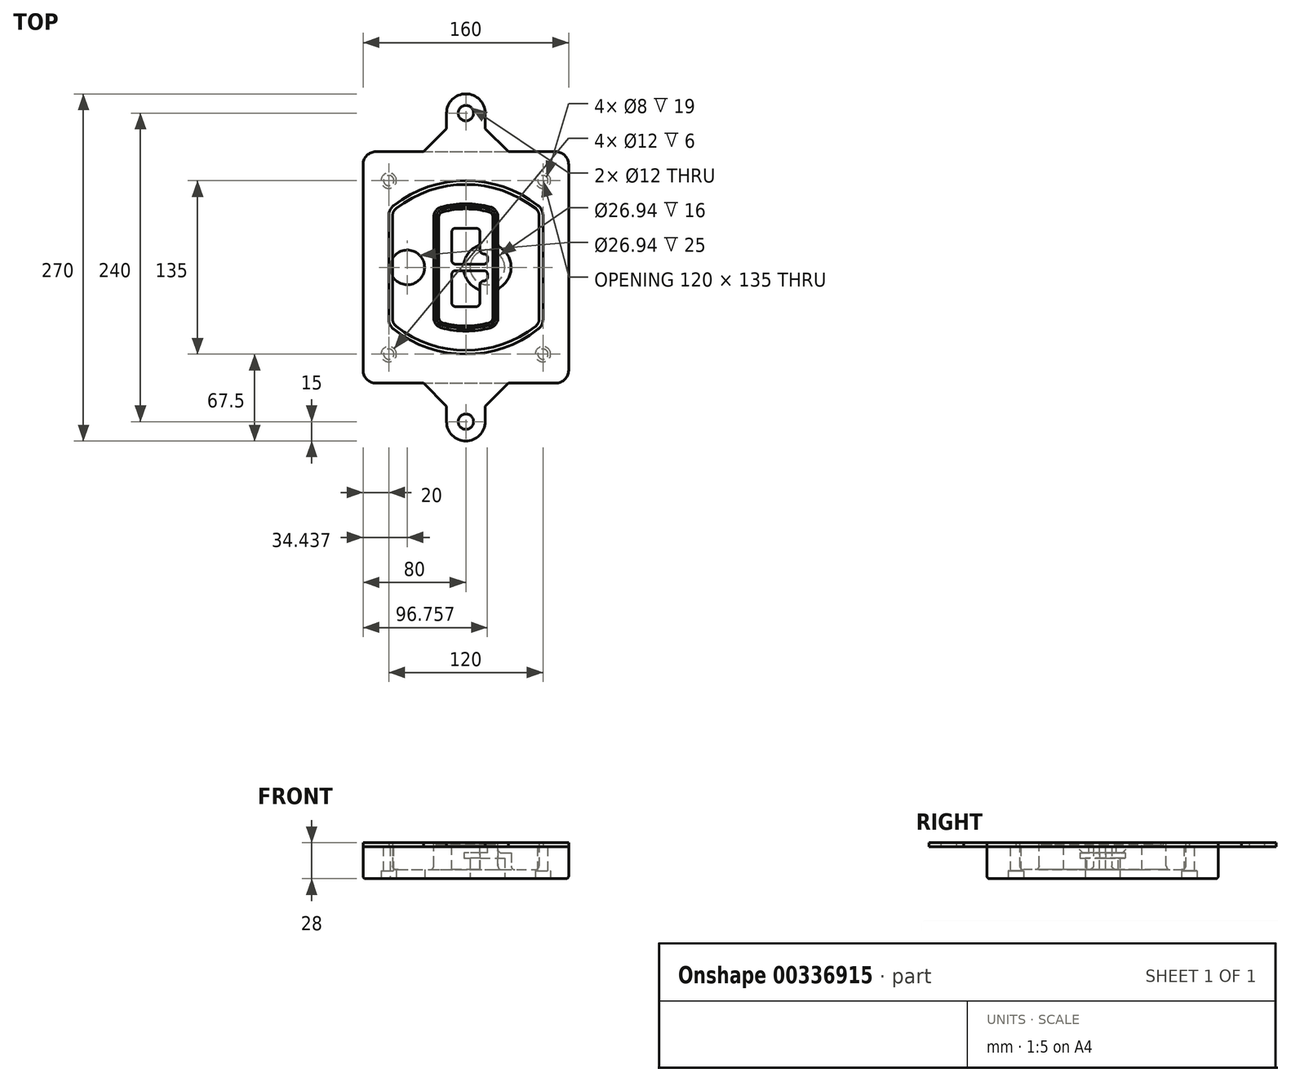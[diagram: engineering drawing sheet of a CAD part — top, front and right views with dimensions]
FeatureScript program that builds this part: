
annotation { "Feature Type Name" : "Feature", "Feature Type Description" : "" }
export const myFeature = defineFeature(function(context is Context, id is Id, definition is map)
    precondition{}
    {
        {
            var Q0;
            Q0=qCreatedBy(makeId("Top.planeOp"),FACE);
            var sketch = newSketch(context, id + "F0", { "sketchPlane" : qUnion([Q0])});
            skPoint(sketch, "E0.rect.middle", {"position": v(0, 0) * mm});
            skLineSegment(sketch, "E1.bottom", {"start": v(-70, -90) * mm, "end": v(70, -90) * mm});
            skLineSegment(sketch, "E1.top", {"start": v(-70, 90) * mm, "end": v(70, 90) * mm});
            skLineSegment(sketch, "E1.left", {"start": v(-80, -80) * mm, "end": v(-80, 80) * mm});
            skLineSegment(sketch, "E1.right", {"start": v(80, -80) * mm, "end": v(80, 80) * mm});
            skLineSegment(sketch, "E2", {"start": v(-80, 90) * mm, "end": v(80, -90) * mm, "construction": true});
            skLineSegment(sketch, "E3", {"start": v(80, 90) * mm, "end": v(-80, -90) * mm, "construction": true});
            skCircle(sketch, "E4", {"center": v(-60, 67.5) * mm, "radius": 4 * mm});
            skCircle(sketch, "E5", {"center": v(60, 67.5) * mm, "radius": 4 * mm});
            skCircle(sketch, "E6", {"center": v(60, -67.5) * mm, "radius": 4 * mm});
            skCircle(sketch, "E7", {"center": v(-60, -67.5) * mm, "radius": 4 * mm});
            skLineSegment(sketch, "E8", {"start": v(-60, 67.5) * mm, "end": v(60, 67.5) * mm, "construction": true});
            skLineSegment(sketch, "E9", {"start": v(60, 67.5) * mm, "end": v(60, -67.5) * mm, "construction": true});
            skLineSegment(sketch, "E10", {"start": v(60, -67.5) * mm, "end": v(-60, -67.5) * mm, "construction": true});
            skLineSegment(sketch, "E11", {"start": v(-60, -67.5) * mm, "end": v(-60, 67.5) * mm, "construction": true});
            skLineSegment(sketch, "E12", {"start": v(-60, 40.3) * mm, "end": v(-60, -40.3) * mm});
            skLineSegment(sketch, "E13", {"start": v(60, 40.3) * mm, "end": v(60, -40.3) * mm});
            skArc(sketch, "E14", {"start": v(56.15, 48.18) * mm, "mid": v(0, 67.5) * mm, "end": v(-56.15, 48.18) * mm});
            skArc(sketch, "E15", {"start": v(-56.15, -48.18) * mm, "mid": v(0, -67.5) * mm, "end": v(56.15, -48.18) * mm});
            skLineSegment(sketch, "E16", {"start": v(-60, 0) * mm, "end": v(60, 0) * mm, "construction": true});
            skPoint(sketch, "E17.visualSharp", {"position": v(-60, -45) * mm});
            skArc(sketch, "E17.filletArc", {"start": v(-60, -40.3) * mm, "mid": v(-58.99, -44.68) * mm, "end": v(-56.15, -48.18) * mm});
            skPoint(sketch, "E18.visualSharp", {"position": v(-60, 45) * mm});
            skArc(sketch, "E18.filletArc", {"start": v(-56.15, 48.18) * mm, "mid": v(-58.99, 44.68) * mm, "end": v(-60, 40.3) * mm});
            skPoint(sketch, "E19.visualSharp", {"position": v(60, 45) * mm});
            skArc(sketch, "E19.filletArc", {"start": v(60, 40.3) * mm, "mid": v(58.99, 44.68) * mm, "end": v(56.15, 48.18) * mm});
            skPoint(sketch, "E20.visualSharp", {"position": v(60, -45) * mm});
            skArc(sketch, "E20.filletArc", {"start": v(56.15, -48.18) * mm, "mid": v(58.99, -44.68) * mm, "end": v(60, -40.3) * mm});
            skPoint(sketch, "E21.visualSharp", {"position": v(-80, 90) * mm});
            skArc(sketch, "E21.filletArc", {"start": v(-70, 90) * mm, "mid": v(-77.07, 87.07) * mm, "end": v(-80, 80) * mm});
            skPoint(sketch, "E22.visualSharp", {"position": v(80, 90) * mm});
            skArc(sketch, "E22.filletArc", {"start": v(80, 80) * mm, "mid": v(77.07, 87.07) * mm, "end": v(70, 90) * mm});
            skPoint(sketch, "E23.visualSharp", {"position": v(80, -90) * mm});
            skArc(sketch, "E23.filletArc", {"start": v(70, -90) * mm, "mid": v(77.07, -87.07) * mm, "end": v(80, -80) * mm});
            skPoint(sketch, "E24.visualSharp", {"position": v(-80, -90) * mm});
            skArc(sketch, "E24.filletArc", {"start": v(-80, -80) * mm, "mid": v(-77.07, -87.07) * mm, "end": v(-70, -90) * mm});
            skArc(sketch, "E25.0", {"start": v(57, 40.3) * mm, "mid": v(56.3, 43.36) * mm, "end": v(54.3, 45.81) * mm});
            skLineSegment(sketch, "E25.1", {"start": v(57, 40.3) * mm, "end": v(57, -40.3) * mm});
            skArc(sketch, "E25.2", {"start": v(54.3, -45.81) * mm, "mid": v(56.3, -43.36) * mm, "end": v(57, -40.3) * mm});
            skArc(sketch, "E25.3", {"start": v(-54.3, -45.81) * mm, "mid": v(0, -64.5) * mm, "end": v(54.3, -45.81) * mm});
            skArc(sketch, "E25.4", {"start": v(-57, -40.3) * mm, "mid": v(-56.3, -43.36) * mm, "end": v(-54.3, -45.81) * mm});
            skArc(sketch, "E25.5", {"start": v(54.3, 45.81) * mm, "mid": v(0, 64.5) * mm, "end": v(-54.3, 45.81) * mm});
            skLineSegment(sketch, "E25.6", {"start": v(-57, 40.3) * mm, "end": v(-57, -40.3) * mm});
            skArc(sketch, "E25.7", {"start": v(-54.3, 45.81) * mm, "mid": v(-56.3, 43.36) * mm, "end": v(-57, 40.3) * mm});
            skArc(sketch, "E26.0", {"start": v(-58.62, 51.33) * mm, "mid": v(-62.58, 46.43) * mm, "end": v(-64, 40.3) * mm});
            skArc(sketch, "E26.1", {"start": v(58.62, 51.33) * mm, "mid": v(0, 71.5) * mm, "end": v(-58.62, 51.33) * mm});
            skArc(sketch, "E26.2", {"start": v(64, 40.3) * mm, "mid": v(62.58, 46.43) * mm, "end": v(58.62, 51.33) * mm});
            skLineSegment(sketch, "E26.3", {"start": v(64, 40.3) * mm, "end": v(64, -40.3) * mm});
            skArc(sketch, "E26.4", {"start": v(58.62, -51.33) * mm, "mid": v(62.58, -46.43) * mm, "end": v(64, -40.3) * mm});
            skLineSegment(sketch, "E26.5", {"start": v(-64, 40.3) * mm, "end": v(-64, -40.3) * mm});
            skArc(sketch, "E26.6", {"start": v(-58.62, -51.33) * mm, "mid": v(0, -71.5) * mm, "end": v(58.62, -51.33) * mm});
            skArc(sketch, "E26.7", {"start": v(-64, -40.3) * mm, "mid": v(-62.58, -46.43) * mm, "end": v(-58.62, -51.33) * mm});
            skSolve(sketch);
        }
        {
            var Q0;
            Q0=makeQuery(id+"F0.imprint","IMPRINT",FACE,{"disambiguationData":[TD([[makeQuery(id+"F0.imprint","IMPRINT",EDGE,{"derivedFrom":sQuery(id+"F0.wireOp",EDGE,"E1.bottom")}),1.0]])]});
            var Q1;
            Q1=makeQuery(id+"F0.imprint","IMPRINT",FACE,{"disambiguationData":[TD([[makeQuery(id+"F0.imprint","IMPRINT",EDGE,{"derivedFrom":sQuery(id+"F0.wireOp",EDGE,"E12")}),1.0]])]});
            var Q2;
            Q2=makeQuery(id+"F0.imprint","IMPRINT",FACE,{"disambiguationData":[TD([[makeQuery(id+"F0.imprint","IMPRINT",EDGE,{"derivedFrom":sQuery(id+"F0.wireOp",EDGE,"E25.0")}),1.0]])]});
            var Q3;
            Q3=makeQuery(id+"F0.imprint","IMPRINT",FACE,{"disambiguationData":[TD([[makeQuery(id+"F0.imprint","IMPRINT",EDGE,{"derivedFrom":sQuery(id+"F0.wireOp",EDGE,"E12")}),-1.0]])]});
            extrude(context, id + "F1", {"entities" : qUnion([Q0, Q1, Q2, Q3]), "oppositeDirection" : true, "depth" : 25 * mm});
        }
        {
            var Q0;
            Q0=makeQuery(id+"F0.imprint","IMPRINT",FACE,{"disambiguationData":[TD([[makeQuery(id+"F0.imprint","IMPRINT",EDGE,{"derivedFrom":sQuery(id+"F0.wireOp",EDGE,"E12")}),1.0]])]});
            extrude(context, id + "F2", {"entities" : qUnion([Q0]), "operationType" : NewBodyOperationType.ADD, "depth" : 3 * mm});
        }
        {
            var Q0;
            Q0=makeQuery(id+"F0.imprint","IMPRINT",FACE,{"disambiguationData":[TD([[makeQuery(id+"F0.imprint","IMPRINT",EDGE,{"derivedFrom":sQuery(id+"F0.wireOp",EDGE,"E25.0")}),1.0]])]});
            extrude(context, id + "F3", {"entities" : qUnion([Q0]), "operationType" : NewBodyOperationType.REMOVE, "oppositeDirection" : true, "depth" : 18 * mm});
        }
        {
            var Q0;
            Q0=makeQuery(id+"F2.opExtrude","CAP_FACE",FACE,{"disambiguationData":[OSD([sQuery(id+"F0.wireOp",EDGE,"E12"),sQuery(id+"F0.wireOp",EDGE,"E13"),sQuery(id+"F0.wireOp",EDGE,"E14"),sQuery(id+"F0.wireOp",EDGE,"E15"),sQuery(id+"F0.wireOp",EDGE,"E17.filletArc"),sQuery(id+"F0.wireOp",EDGE,"E18.filletArc"),sQuery(id+"F0.wireOp",EDGE,"E19.filletArc"),sQuery(id+"F0.wireOp",EDGE,"E20.filletArc"),sQuery(id+"F0.wireOp",EDGE,"E25.0"),sQuery(id+"F0.wireOp",EDGE,"E25.1"),sQuery(id+"F0.wireOp",EDGE,"E25.2"),sQuery(id+"F0.wireOp",EDGE,"E25.3"),sQuery(id+"F0.wireOp",EDGE,"E25.4"),sQuery(id+"F0.wireOp",EDGE,"E25.5"),sQuery(id+"F0.wireOp",EDGE,"E25.6"),sQuery(id+"F0.wireOp",EDGE,"E25.7")])],"isStart":false});
            var sketch = newSketch(context, id + "F4", { "sketchPlane" : qUnion([Q0])});
            skArc(sketch, "E27.0", {"start": v(-19.08, -46.97) * mm, "mid": v(0, -49.5) * mm, "end": v(19.08, -46.97) * mm});
            skArc(sketch, "E28.0", {"start": v(19.08, 46.97) * mm, "mid": v(0, 49.5) * mm, "end": v(-19.08, 46.97) * mm});
            skLineSegment(sketch, "E29", {"start": v(-25, 39.25) * mm, "end": v(-25, -39.25) * mm});
            skLineSegment(sketch, "E30", {"start": v(25, 39.25) * mm, "end": v(25, -39.25) * mm});
            skLineSegment(sketch, "E31", {"start": v(-25, 45.1) * mm, "end": v(25, 45.1) * mm, "construction": true});
            skLineSegment(sketch, "E32", {"start": v(-25, -45.1) * mm, "end": v(25, -45.1) * mm, "construction": true});
            skPoint(sketch, "E33.visualSharp", {"position": v(-25, 45.1) * mm});
            skArc(sketch, "E33.filletArc", {"start": v(-19.08, 46.97) * mm, "mid": v(-23.35, 44.11) * mm, "end": v(-25, 39.25) * mm});
            skPoint(sketch, "E34.visualSharp", {"position": v(25, 45.1) * mm});
            skArc(sketch, "E34.filletArc", {"start": v(25, 39.25) * mm, "mid": v(23.35, 44.11) * mm, "end": v(19.08, 46.97) * mm});
            skPoint(sketch, "E35.visualSharp", {"position": v(25, -45.1) * mm});
            skArc(sketch, "E35.filletArc", {"start": v(19.08, -46.97) * mm, "mid": v(23.35, -44.11) * mm, "end": v(25, -39.25) * mm});
            skPoint(sketch, "E36.visualSharp", {"position": v(-25, -45.1) * mm});
            skArc(sketch, "E36.filletArc", {"start": v(-25, -39.25) * mm, "mid": v(-23.35, -44.11) * mm, "end": v(-19.08, -46.97) * mm});
            skArc(sketch, "E37.0", {"start": v(54.3, 45.81) * mm, "mid": v(0, 64.5) * mm, "end": v(-54.3, 45.81) * mm});
            skArc(sketch, "E37.1", {"start": v(-54.3, 45.81) * mm, "mid": v(-56.3, 43.36) * mm, "end": v(-57, 40.3) * mm});
            skLineSegment(sketch, "E37.2", {"start": v(-57, 40.3) * mm, "end": v(-57, -40.3) * mm});
            skArc(sketch, "E37.3", {"start": v(-57, -40.3) * mm, "mid": v(-56.3, -43.36) * mm, "end": v(-54.3, -45.81) * mm});
            skArc(sketch, "E37.4", {"start": v(-54.3, -45.81) * mm, "mid": v(0, -64.5) * mm, "end": v(54.3, -45.81) * mm});
            skArc(sketch, "E37.5", {"start": v(54.3, -45.81) * mm, "mid": v(56.3, -43.36) * mm, "end": v(57, -40.3) * mm});
            skLineSegment(sketch, "E37.6", {"start": v(57, 40.3) * mm, "end": v(57, -40.3) * mm});
            skArc(sketch, "E37.7", {"start": v(57, 40.3) * mm, "mid": v(56.3, 43.36) * mm, "end": v(54.3, 45.81) * mm});
            skLineSegment(sketch, "E38.0", {"start": v(23, 39.25) * mm, "end": v(23, -39.25) * mm});
            skArc(sketch, "E38.1", {"start": v(18.56, -45.04) * mm, "mid": v(21.76, -42.9) * mm, "end": v(23, -39.25) * mm});
            skArc(sketch, "E38.2", {"start": v(-18.56, -45.04) * mm, "mid": v(0, -47.5) * mm, "end": v(18.56, -45.04) * mm});
            skArc(sketch, "E38.3", {"start": v(-23, -39.25) * mm, "mid": v(-21.76, -42.9) * mm, "end": v(-18.56, -45.04) * mm});
            skLineSegment(sketch, "E38.4", {"start": v(-23, 39.25) * mm, "end": v(-23, -39.25) * mm});
            skArc(sketch, "E38.5", {"start": v(23, 39.25) * mm, "mid": v(21.76, 42.9) * mm, "end": v(18.56, 45.04) * mm});
            skArc(sketch, "E38.6", {"start": v(-18.56, 45.04) * mm, "mid": v(-21.76, 42.9) * mm, "end": v(-23, 39.25) * mm});
            skArc(sketch, "E38.7", {"start": v(18.56, 45.04) * mm, "mid": v(0, 47.5) * mm, "end": v(-18.56, 45.04) * mm});
            skArc(sketch, "E39.0", {"start": v(21, 39.25) * mm, "mid": v(20.18, 41.68) * mm, "end": v(18.04, 43.1) * mm});
            skLineSegment(sketch, "E39.1", {"start": v(21, 39.25) * mm, "end": v(21, -39.25) * mm});
            skArc(sketch, "E39.2", {"start": v(18.04, -43.1) * mm, "mid": v(20.18, -41.68) * mm, "end": v(21, -39.25) * mm});
            skArc(sketch, "E39.3", {"start": v(-18.04, -43.1) * mm, "mid": v(0, -45.5) * mm, "end": v(18.04, -43.1) * mm});
            skArc(sketch, "E39.4", {"start": v(-21, -39.25) * mm, "mid": v(-20.18, -41.68) * mm, "end": v(-18.04, -43.1) * mm});
            skArc(sketch, "E39.5", {"start": v(18.04, 43.1) * mm, "mid": v(0, 45.5) * mm, "end": v(-18.04, 43.1) * mm});
            skLineSegment(sketch, "E39.6", {"start": v(-21, 39.25) * mm, "end": v(-21, -39.25) * mm});
            skArc(sketch, "E39.7", {"start": v(-18.04, 43.1) * mm, "mid": v(-20.18, 41.68) * mm, "end": v(-21, 39.25) * mm});
            skLineSegment(sketch, "E40", {"start": v(-25, 0) * mm, "end": v(25, 0) * mm, "construction": true});
            skLineSegment(sketch, "E41", {"start": v(-11, 5.5) * mm, "end": v(-11, 27.5) * mm});
            skLineSegment(sketch, "E42", {"start": v(-8, 30.5) * mm, "end": v(8, 30.5) * mm});
            skLineSegment(sketch, "E43", {"start": v(11, 27.5) * mm, "end": v(11, 13.5) * mm});
            skLineSegment(sketch, "E44", {"start": v(14, 10.5) * mm, "end": v(14, 10.5) * mm});
            skLineSegment(sketch, "E45", {"start": v(17, 7.5) * mm, "end": v(17, 5.5) * mm});
            skLineSegment(sketch, "E46", {"start": v(14, 2.5) * mm, "end": v(-8, 2.5) * mm});
            skPoint(sketch, "E47.visualSharp", {"position": v(-11, 30.5) * mm});
            skArc(sketch, "E47.filletArc", {"start": v(-8, 30.5) * mm, "mid": v(-10.12, 29.62) * mm, "end": v(-11, 27.5) * mm});
            skPoint(sketch, "E48.visualSharp", {"position": v(11, 30.5) * mm});
            skArc(sketch, "E48.filletArc", {"start": v(11, 27.5) * mm, "mid": v(10.12, 29.62) * mm, "end": v(8, 30.5) * mm});
            skPoint(sketch, "E49.visualSharp", {"position": v(11, 10.5) * mm});
            skArc(sketch, "E49.filletArc", {"start": v(11, 13.5) * mm, "mid": v(11.88, 11.38) * mm, "end": v(14, 10.5) * mm});
            skPoint(sketch, "E50.visualSharp", {"position": v(17, 10.5) * mm});
            skArc(sketch, "E50.filletArc", {"start": v(17, 7.5) * mm, "mid": v(16.12, 9.62) * mm, "end": v(14, 10.5) * mm});
            skPoint(sketch, "E51.visualSharp", {"position": v(17, 2.5) * mm});
            skArc(sketch, "E51.filletArc", {"start": v(14, 2.5) * mm, "mid": v(16.12, 3.38) * mm, "end": v(17, 5.5) * mm});
            skPoint(sketch, "E52.visualSharp", {"position": v(-11, 2.5) * mm});
            skArc(sketch, "E52.filletArc", {"start": v(-11, 5.5) * mm, "mid": v(-10.12, 3.38) * mm, "end": v(-8, 2.5) * mm});
            skLineSegment(sketch, "E53.0.MirrorCS", {"start": v(14, -2.5) * mm, "end": v(-8, -2.5) * mm});
            skArc(sketch, "E54.0.MirrorCS", {"start": v(-11, -5.5) * mm, "mid": v(-10.12, -3.38) * mm, "end": v(-8, -2.5) * mm});
            skLineSegment(sketch, "E55.0.MirrorCS", {"start": v(-11, -5.5) * mm, "end": v(-11, -27.5) * mm});
            skArc(sketch, "E56.0.MirrorCS", {"start": v(-8, -30.5) * mm, "mid": v(-10.12, -29.62) * mm, "end": v(-11, -27.5) * mm});
            skLineSegment(sketch, "E57.0.MirrorCS", {"start": v(-8, -30.5) * mm, "end": v(8, -30.5) * mm});
            skArc(sketch, "E58.0.MirrorCS", {"start": v(11, -27.5) * mm, "mid": v(10.12, -29.62) * mm, "end": v(8, -30.5) * mm});
            skLineSegment(sketch, "E59.0.MirrorCS", {"start": v(11, -27.5) * mm, "end": v(11, -13.5) * mm});
            skArc(sketch, "E60.0.MirrorCS", {"start": v(11, -13.5) * mm, "mid": v(11.88, -11.38) * mm, "end": v(14, -10.5) * mm});
            skArc(sketch, "E61.0.MirrorCS", {"start": v(17, -7.5) * mm, "mid": v(16.12, -9.62) * mm, "end": v(14, -10.5) * mm});
            skLineSegment(sketch, "E62.0.MirrorCS", {"start": v(17, -7.5) * mm, "end": v(17, -5.5) * mm});
            skArc(sketch, "E63.0.MirrorCS", {"start": v(14, -2.5) * mm, "mid": v(16.12, -3.38) * mm, "end": v(17, -5.5) * mm});
            skSolve(sketch);
        }
        {
            var Q0;
            Q0=makeQuery(id+"F4.imprint","IMPRINT",FACE,{"disambiguationData":[TD([[makeQuery(id+"F4.imprint","IMPRINT",EDGE,{"derivedFrom":sQuery(id+"F4.wireOp",EDGE,"E27.0")}),1.0]])]});
            var Q1;
            Q1=makeQuery(id+"F4.imprint","IMPRINT",FACE,{"disambiguationData":[TD([[makeQuery(id+"F4.imprint","IMPRINT",EDGE,{"derivedFrom":sQuery(id+"F4.wireOp",EDGE,"E38.0")}),-1.0]])]});
            var Q2;
            Q2=makeQuery(id+"F4.imprint","IMPRINT",FACE,{"disambiguationData":[TD([[makeQuery(id+"F4.imprint","IMPRINT",EDGE,{"derivedFrom":sQuery(id+"F4.wireOp",EDGE,"E39.0")}),1.0]])]});
            extrude(context, id + "F5", {"entities" : qUnion([Q0, Q1, Q2]), "operationType" : NewBodyOperationType.ADD, "endBound" : BoundingType.UP_TO_NEXT, "oppositeDirection" : true, "depth" : 25 * mm});
        }
        {
            var Q0;
            Q0=makeQuery(id+"F4.imprint","IMPRINT",FACE,{"disambiguationData":[TD([[makeQuery(id+"F4.imprint","IMPRINT",EDGE,{"derivedFrom":sQuery(id+"F4.wireOp",EDGE,"E38.0")}),-1.0]])]});
            extrude(context, id + "F6", {"entities" : qUnion([Q0]), "operationType" : NewBodyOperationType.REMOVE, "oppositeDirection" : true, "depth" : 2 * mm});
        }
        {
            var Q0;
            Q0=makeQuery(id+"F1.opExtrude","CAP_FACE",FACE,{"disambiguationData":[OSD([sQuery(id+"F0.wireOp",EDGE,"E1.bottom"),sQuery(id+"F0.wireOp",EDGE,"E1.top"),sQuery(id+"F0.wireOp",EDGE,"E1.left"),sQuery(id+"F0.wireOp",EDGE,"E1.right"),sQuery(id+"F0.wireOp",EDGE,"E4"),sQuery(id+"F0.wireOp",EDGE,"E5"),sQuery(id+"F0.wireOp",EDGE,"E6"),sQuery(id+"F0.wireOp",EDGE,"E7"),sQuery(id+"F0.wireOp",EDGE,"E21.filletArc"),sQuery(id+"F0.wireOp",EDGE,"E22.filletArc"),sQuery(id+"F0.wireOp",EDGE,"E23.filletArc"),sQuery(id+"F0.wireOp",EDGE,"E24.filletArc")])],"isStart":false});
            var sketch = newSketch(context, id + "F7", { "sketchPlane" : qUnion([Q0])});
            skCircle(sketch, "E64", {"center": v(16.76, 0) * mm, "radius": 13.47 * mm});
            skCircle(sketch, "E65", {"center": v(-45.56, 0) * mm, "radius": 13.47 * mm});
            skLineSegment(sketch, "E66", {"start": v(80, 0) * mm, "end": v(-80, 0) * mm});
            skCircle(sketch, "E67", {"center": v(16.76, 0) * mm, "radius": 18.47 * mm});
            skCircle(sketch, "E68", {"center": v(60, -67.5) * mm, "radius": 6 * mm});
            skCircle(sketch, "E69", {"center": v(-60, -67.5) * mm, "radius": 6 * mm});
            skCircle(sketch, "E70", {"center": v(-60, 67.5) * mm, "radius": 6 * mm});
            skCircle(sketch, "E71", {"center": v(60, 67.5) * mm, "radius": 6 * mm});
            skSolve(sketch);
        }
        {
            var Q0;
            {var subQ1=sQuery(id+"F7.wireOp",EDGE,"E66");var subQ4=sQuery(id+"F7.wireOp",EDGE,"E64");var subQ6=makeQuery(id+"F7.imprint","INTERSECT",VERTEX,{"disambiguationData":[OD(0.0)],"derivedFrom":[subQ4,subQ1]});Q0=makeQuery(id+"F7.imprint","IMPRINT",FACE,{"disambiguationData":[TD([[makeQuery(id+"F7.imprint","IMPRINT",EDGE,{"disambiguationData":[TD([[subQ6,-1.0]])],"derivedFrom":subQ4}),-1.0]])]});}
            var Q1;
            {var subQ0=sQuery(id+"F7.wireOp",EDGE,"E66");var subQ1=sQuery(id+"F7.wireOp",EDGE,"E64");var subQ3=makeQuery(id+"F7.imprint","INTERSECT",VERTEX,{"disambiguationData":[OD(0.0)],"derivedFrom":[subQ1,subQ0]});Q1=makeQuery(id+"F7.imprint","IMPRINT",FACE,{"disambiguationData":[TD([[makeQuery(id+"F7.imprint","IMPRINT",EDGE,{"disambiguationData":[TD([[subQ3,-1.0]])],"derivedFrom":subQ1}),1.0]])]});}
            var Q2;
            {var subQ0=sQuery(id+"F7.wireOp",EDGE,"E66");var subQ1=sQuery(id+"F7.wireOp",EDGE,"E64");var subQ3=makeQuery(id+"F7.imprint","INTERSECT",VERTEX,{"disambiguationData":[OD(0.0)],"derivedFrom":[subQ1,subQ0]});Q2=makeQuery(id+"F7.imprint","IMPRINT",FACE,{"disambiguationData":[TD([[makeQuery(id+"F7.imprint","IMPRINT",EDGE,{"disambiguationData":[TD([[subQ3,1.0]])],"derivedFrom":subQ1}),1.0]])]});}
            var Q3;
            {var subQ1=sQuery(id+"F7.wireOp",EDGE,"E66");var subQ4=sQuery(id+"F7.wireOp",EDGE,"E64");var subQ6=makeQuery(id+"F7.imprint","INTERSECT",VERTEX,{"disambiguationData":[OD(0.0)],"derivedFrom":[subQ4,subQ1]});Q3=makeQuery(id+"F7.imprint","IMPRINT",FACE,{"disambiguationData":[TD([[makeQuery(id+"F7.imprint","IMPRINT",EDGE,{"disambiguationData":[TD([[subQ6,1.0]])],"derivedFrom":subQ4}),-1.0]])]});}
            extrude(context, id + "F8", {"entities" : qUnion([Q0, Q1, Q2, Q3]), "operationType" : NewBodyOperationType.ADD, "oppositeDirection" : true, "depth" : 20 * mm});
        }
        {
            var Q0;
            {var subQ0=sQuery(id+"F7.wireOp",EDGE,"E66");var subQ1=sQuery(id+"F7.wireOp",EDGE,"E64");var subQ3=makeQuery(id+"F7.imprint","INTERSECT",VERTEX,{"disambiguationData":[OD(0.0)],"derivedFrom":[subQ1,subQ0]});Q0=makeQuery(id+"F7.imprint","IMPRINT",FACE,{"disambiguationData":[TD([[makeQuery(id+"F7.imprint","IMPRINT",EDGE,{"disambiguationData":[TD([[subQ3,-1.0]])],"derivedFrom":subQ1}),1.0]])]});}
            var Q1;
            {var subQ0=sQuery(id+"F7.wireOp",EDGE,"E66");var subQ1=sQuery(id+"F7.wireOp",EDGE,"E64");var subQ3=makeQuery(id+"F7.imprint","INTERSECT",VERTEX,{"disambiguationData":[OD(0.0)],"derivedFrom":[subQ1,subQ0]});Q1=makeQuery(id+"F7.imprint","IMPRINT",FACE,{"disambiguationData":[TD([[makeQuery(id+"F7.imprint","IMPRINT",EDGE,{"disambiguationData":[TD([[subQ3,1.0]])],"derivedFrom":subQ1}),1.0]])]});}
            extrude(context, id + "F9", {"entities" : qUnion([Q0, Q1]), "operationType" : NewBodyOperationType.REMOVE, "oppositeDirection" : true, "depth" : 16 * mm});
        }
        {
            var Q0;
            {var subQ0=sQuery(id+"F7.wireOp",EDGE,"E66");var subQ1=sQuery(id+"F7.wireOp",EDGE,"E65");var subQ3=makeQuery(id+"F7.imprint","INTERSECT",VERTEX,{"disambiguationData":[OD(0.0)],"derivedFrom":[subQ1,subQ0]});Q0=makeQuery(id+"F7.imprint","IMPRINT",FACE,{"disambiguationData":[TD([[makeQuery(id+"F7.imprint","IMPRINT",EDGE,{"disambiguationData":[TD([[subQ3,-1.0]])],"derivedFrom":subQ1}),1.0]])]});}
            var Q1;
            {var subQ0=sQuery(id+"F7.wireOp",EDGE,"E66");var subQ1=sQuery(id+"F7.wireOp",EDGE,"E65");var subQ3=makeQuery(id+"F7.imprint","INTERSECT",VERTEX,{"disambiguationData":[OD(0.0)],"derivedFrom":[subQ1,subQ0]});Q1=makeQuery(id+"F7.imprint","IMPRINT",FACE,{"disambiguationData":[TD([[makeQuery(id+"F7.imprint","IMPRINT",EDGE,{"disambiguationData":[TD([[subQ3,1.0]])],"derivedFrom":subQ1}),1.0]])]});}
            extrude(context, id + "F10", {"entities" : qUnion([Q0, Q1]), "operationType" : NewBodyOperationType.REMOVE, "oppositeDirection" : true, "depth" : 25 * mm});
        }
        {
            var Q0;
            Q0=makeQuery(id+"F7.imprint","IMPRINT",FACE,{"disambiguationData":[TD([[makeQuery(id+"F7.imprint","IMPRINT",EDGE,{"derivedFrom":sQuery(id+"F7.wireOp",EDGE,"E68")}),1.0]])]});
            var Q1;
            Q1=makeQuery(id+"F7.imprint","IMPRINT",FACE,{"disambiguationData":[TD([[makeQuery(id+"F7.imprint","IMPRINT",EDGE,{"derivedFrom":makeQuery(id+"F1.opExtrude","CAP_EDGE",EDGE,{"disambiguationData":[OSD([sQuery(id+"F0.wireOp",EDGE,"E5")])],"isStart":false})}),-1.0]])]});
            var Q2;
            Q2=makeQuery(id+"F7.imprint","IMPRINT",FACE,{"disambiguationData":[TD([[makeQuery(id+"F7.imprint","IMPRINT",EDGE,{"derivedFrom":sQuery(id+"F7.wireOp",EDGE,"E69")}),1.0]])]});
            var Q3;
            Q3=makeQuery(id+"F7.imprint","IMPRINT",FACE,{"disambiguationData":[TD([[makeQuery(id+"F7.imprint","IMPRINT",EDGE,{"derivedFrom":makeQuery(id+"F1.opExtrude","CAP_EDGE",EDGE,{"disambiguationData":[OSD([sQuery(id+"F0.wireOp",EDGE,"E4")])],"isStart":false})}),-1.0]])]});
            var Q4;
            Q4=makeQuery(id+"F7.imprint","IMPRINT",FACE,{"disambiguationData":[TD([[makeQuery(id+"F7.imprint","IMPRINT",EDGE,{"derivedFrom":sQuery(id+"F7.wireOp",EDGE,"E70")}),1.0]])]});
            var Q5;
            Q5=makeQuery(id+"F7.imprint","IMPRINT",FACE,{"disambiguationData":[TD([[makeQuery(id+"F7.imprint","IMPRINT",EDGE,{"derivedFrom":makeQuery(id+"F1.opExtrude","CAP_EDGE",EDGE,{"disambiguationData":[OSD([sQuery(id+"F0.wireOp",EDGE,"E7")])],"isStart":false})}),-1.0]])]});
            var Q6;
            Q6=makeQuery(id+"F7.imprint","IMPRINT",FACE,{"disambiguationData":[TD([[makeQuery(id+"F7.imprint","IMPRINT",EDGE,{"derivedFrom":sQuery(id+"F7.wireOp",EDGE,"E71")}),1.0]])]});
            var Q7;
            Q7=makeQuery(id+"F7.imprint","IMPRINT",FACE,{"disambiguationData":[TD([[makeQuery(id+"F7.imprint","IMPRINT",EDGE,{"derivedFrom":makeQuery(id+"F1.opExtrude","CAP_EDGE",EDGE,{"disambiguationData":[OSD([sQuery(id+"F0.wireOp",EDGE,"E6")])],"isStart":false})}),-1.0]])]});
            extrude(context, id + "F11", {"entities" : qUnion([Q0, Q1, Q2, Q3, Q4, Q5, Q6, Q7]), "operationType" : NewBodyOperationType.REMOVE, "oppositeDirection" : true, "depth" : 6 * mm});
        }
        {
            var Q0;
            Q0=makeQuery(id+"F9.boolean.opBoolean","COPY",FACE,{"derivedFrom":makeQuery(id+"F9.opExtrude","CAP_FACE",FACE,{"disambiguationData":[OSD([sQuery(id+"F7.wireOp",EDGE,"E64")])],"isStart":false})});
            var sketch = newSketch(context, id + "F12", { "sketchPlane" : qUnion([Q0])});
            skArc(sketch, "E72.0", {"start": v(11, 17.55) * mm, "mid": v(2.57, 11.82) * mm, "end": v(-1.54, 2.5) * mm});
            skArc(sketch, "E72.1", {"start": v(-1.54, -2.5) * mm, "mid": v(2.57, -11.82) * mm, "end": v(11, -17.55) * mm});
            skLineSegment(sketch, "E73", {"start": v(-1.54, -2.5) * mm, "end": v(14, -2.5) * mm});
            skLineSegment(sketch, "E74.0", {"start": v(14, 2.5) * mm, "end": v(-1.54, 2.5) * mm});
            skArc(sketch, "E74.1", {"start": v(14, 2.5) * mm, "mid": v(16.12, 3.38) * mm, "end": v(17, 5.5) * mm});
            skLineSegment(sketch, "E74.2", {"start": v(17, 7.5) * mm, "end": v(17, 5.5) * mm});
            skArc(sketch, "E74.3", {"start": v(17, 7.5) * mm, "mid": v(16.12, 9.62) * mm, "end": v(14, 10.5) * mm});
            skArc(sketch, "E74.4", {"start": v(11, 13.5) * mm, "mid": v(11.88, 11.38) * mm, "end": v(14, 10.5) * mm});
            skLineSegment(sketch, "E74.5", {"start": v(11, 17.55) * mm, "end": v(11, 13.5) * mm});
            skLineSegment(sketch, "E74.7", {"start": v(14, -2.5) * mm, "end": v(-1.54, -2.5) * mm});
            skArc(sketch, "E74.8", {"start": v(14, -2.5) * mm, "mid": v(16.12, -3.38) * mm, "end": v(17, -5.5) * mm});
            skLineSegment(sketch, "E74.9", {"start": v(17, -7.5) * mm, "end": v(17, -5.5) * mm});
            skArc(sketch, "E74.10", {"start": v(17, -7.5) * mm, "mid": v(16.12, -9.62) * mm, "end": v(14, -10.5) * mm});
            skArc(sketch, "E74.11", {"start": v(11, -13.5) * mm, "mid": v(11.88, -11.38) * mm, "end": v(14, -10.5) * mm});
            skLineSegment(sketch, "E74.12", {"start": v(11, -17.55) * mm, "end": v(11, -13.5) * mm});
            skPoint(sketch, "E75.orphan", {"position": v(11, -27.5) * mm});
            skPoint(sketch, "E76.orphan", {"position": v(-8, -2.5) * mm});
            skPoint(sketch, "E77.orphan", {"position": v(-8, 2.5) * mm});
            skPoint(sketch, "E78.orphan", {"position": v(11, 27.5) * mm});
            skSolve(sketch);
        }
        {
            var Q0;
            {var subQ7=sQuery(id+"F12.wireOp",EDGE,"E72.0");var subQ14=sQuery(id+"F12.wireOp",EDGE,"E72.1");var subQ16=sQuery(id+"F12.wireOp",EDGE,"E74.1");var subQ18=sQuery(id+"F12.wireOp",EDGE,"E74.8");Q0=qUnion([makeQuery(id+"F12.imprint","IMPRINT",FACE,{"disambiguationData":[TD([[makeQuery(id+"F12.imprint","IMPRINT",EDGE,{"derivedFrom":subQ7}),1.0]])]}),makeQuery(id+"F12.imprint","IMPRINT",FACE,{"disambiguationData":[TD([[makeQuery(id+"F12.imprint","IMPRINT",EDGE,{"derivedFrom":subQ14}),1.0]])]}),makeQuery(id+"F12.imprint","IMPRINT",FACE,{"disambiguationData":[TD([[makeQuery(id+"F12.imprint","IMPRINT",EDGE,{"derivedFrom":subQ16}),1.0]])]}),makeQuery(id+"F12.imprint","IMPRINT",FACE,{"disambiguationData":[TD([[makeQuery(id+"F12.imprint","IMPRINT",EDGE,{"derivedFrom":subQ18}),-1.0]])]})]);}
            var Q1;
            Q1=makeQuery(id+"F5.boolean.opBoolean","SPLIT",FACE,{"disambiguationData":[TD([makeQuery(id+"F5.opExtrude","SWEPT_FACE",FACE,{"disambiguationData":[OSD([sQuery(id+"F4.wireOp",EDGE,"E41")])]})])],"derivedFrom":makeQuery(id+"F3.boolean.opBoolean","COPY",FACE,{"derivedFrom":makeQuery(id+"F3.opExtrude","CAP_FACE",FACE,{"disambiguationData":[OSD([sQuery(id+"F0.wireOp",EDGE,"E25.0"),sQuery(id+"F0.wireOp",EDGE,"E25.1"),sQuery(id+"F0.wireOp",EDGE,"E25.2"),sQuery(id+"F0.wireOp",EDGE,"E25.3"),sQuery(id+"F0.wireOp",EDGE,"E25.4"),sQuery(id+"F0.wireOp",EDGE,"E25.5"),sQuery(id+"F0.wireOp",EDGE,"E25.6"),sQuery(id+"F0.wireOp",EDGE,"E25.7")])],"isStart":false})})});
            extrude(context, id + "F13", {"entities" : qUnion([Q0]), "operationType" : NewBodyOperationType.REMOVE, "endBound" : BoundingType.UP_TO_SURFACE, "endBoundEntityFace" : qUnion([Q1]), "depth" : 25 * mm});
        }
        {
            var Q0;
            Q0=makeQuery(id+"F3.boolean.opBoolean","COPY",EDGE,{"derivedFrom":makeQuery(id+"F3.opExtrude","CAP_EDGE",EDGE,{"disambiguationData":[OSD([sQuery(id+"F0.wireOp",EDGE,"E25.6")])],"isStart":false})});
            var Q1;
            Q1=makeQuery(id+"F8.boolean.opBoolean","INTERSECT",EDGE,{"derivedFrom":[makeQuery(id+"F5.opExtrude","SWEPT_FACE",FACE,{"disambiguationData":[OSD([sQuery(id+"F4.wireOp",EDGE,"E30")])]}),makeQuery(id+"F8.opExtrude","CAP_FACE",FACE,{"disambiguationData":[OSD([sQuery(id+"F7.wireOp",EDGE,"E67")])],"isStart":false})]});
            var Q2;
            Q2=makeQuery(id+"F8.boolean.opBoolean","INTERSECT",EDGE,{"disambiguationData":[OD(1.0)],"derivedFrom":[makeQuery(id+"F5.opExtrude","SWEPT_FACE",FACE,{"disambiguationData":[OSD([sQuery(id+"F4.wireOp",EDGE,"E30")])]}),makeQuery(id+"F8.opExtrude","SWEPT_FACE",FACE,{"disambiguationData":[OSD([sQuery(id+"F7.wireOp",EDGE,"E67")])]})]});
            var Q3;
            {var subQ0=sQuery(id+"F4.wireOp",EDGE,"E30");Q3=makeQuery(id+"F8.boolean.opBoolean","SPLIT",EDGE,{"disambiguationData":[TD([makeQuery(id+"F5.opExtrude","SWEPT_FACE",FACE,{"disambiguationData":[OSD([sQuery(id+"F4.wireOp",EDGE,"E35.filletArc")])]})])],"derivedFrom":makeQuery(id+"F5.opExtrude","CAP_EDGE",EDGE,{"disambiguationData":[OSD([subQ0])],"isStart":false})});}
            var Q4;
            {var subQ0=sQuery(id+"F0.wireOp",EDGE,"E25.7");var subQ1=sQuery(id+"F0.wireOp",EDGE,"E25.1");var subQ2=sQuery(id+"F0.wireOp",EDGE,"E25.6");var subQ3=sQuery(id+"F0.wireOp",EDGE,"E25.5");var subQ4=sQuery(id+"F0.wireOp",EDGE,"E25.4");var subQ5=sQuery(id+"F0.wireOp",EDGE,"E25.0");var subQ6=sQuery(id+"F0.wireOp",EDGE,"E25.2");var subQ7=sQuery(id+"F0.wireOp",EDGE,"E25.3");Q4=makeQuery(id+"F8.boolean.opBoolean","INTERSECT",EDGE,{"derivedFrom":[makeQuery(id+"F5.boolean.opBoolean","SPLIT",FACE,{"disambiguationData":[TD([makeQuery(id+"F2.opExtrude","SWEPT_FACE",FACE,{"disambiguationData":[OSD([subQ5])]})])],"derivedFrom":makeQuery(id+"F3.boolean.opBoolean","COPY",FACE,{"derivedFrom":makeQuery(id+"F3.opExtrude","CAP_FACE",FACE,{"disambiguationData":[OSD([subQ5,subQ1,subQ6,subQ7,subQ4,subQ3,subQ2,subQ0])],"isStart":false})})}),makeQuery(id+"F8.opExtrude","SWEPT_FACE",FACE,{"disambiguationData":[OSD([sQuery(id+"F7.wireOp",EDGE,"E67")])]})]});}
            var Q5;
            Q5=makeQuery(id+"F8.boolean.opBoolean","INTERSECT",EDGE,{"disambiguationData":[OD(0.0)],"derivedFrom":[makeQuery(id+"F5.opExtrude","SWEPT_FACE",FACE,{"disambiguationData":[OSD([sQuery(id+"F4.wireOp",EDGE,"E30")])]}),makeQuery(id+"F8.opExtrude","SWEPT_FACE",FACE,{"disambiguationData":[OSD([sQuery(id+"F7.wireOp",EDGE,"E67")])]})]});
            fillet(context, id + "F14", {"entities" : qUnion([Q0, Q1, Q2, Q3, Q4, Q5]), "radius" : 3 * mm, "tangentPropagation" : true, "allowEdgeOverflow" : false});
        }
        {
            var Q0;
            Q0=makeQuery(id+"F1.opExtrude","CAP_EDGE",EDGE,{"disambiguationData":[OSD([sQuery(id+"F0.wireOp",EDGE,"E1.bottom")])],"isStart":false});
            fillet(context, id + "F15", {"entities" : qUnion([Q0]), "radius" : 2 * mm, "tangentPropagation" : true, "allowEdgeOverflow" : false});
        }
        {
            var Q0;
            {var subQ0=sQuery(id+"F0.wireOp",EDGE,"E21.filletArc");var subQ1=sQuery(id+"F0.wireOp",EDGE,"E7");var subQ2=sQuery(id+"F0.wireOp",EDGE,"E6");var subQ3=sQuery(id+"F0.wireOp",EDGE,"E5");var subQ4=sQuery(id+"F0.wireOp",EDGE,"E4");var subQ5=sQuery(id+"F0.wireOp",EDGE,"E22.filletArc");var subQ6=sQuery(id+"F0.wireOp",EDGE,"E1.bottom");var subQ7=sQuery(id+"F0.wireOp",EDGE,"E1.right");var subQ8=sQuery(id+"F0.wireOp",EDGE,"E1.top");var subQ9=sQuery(id+"F0.wireOp",EDGE,"E1.left");var subQ10=sQuery(id+"F0.wireOp",EDGE,"E23.filletArc");var subQ11=sQuery(id+"F0.wireOp",EDGE,"E24.filletArc");Q0=makeQuery(id+"F2.boolean.opBoolean","SPLIT",FACE,{"disambiguationData":[TD([makeQuery(id+"F1.opExtrude","SWEPT_FACE",FACE,{"disambiguationData":[OSD([subQ6])]})])],"derivedFrom":makeQuery(id+"F1.opExtrude","CAP_FACE",FACE,{"disambiguationData":[OSD([subQ6,subQ8,subQ9,subQ7,subQ4,subQ3,subQ2,subQ1,subQ0,subQ5,subQ10,subQ11])],"isStart":true})});}
            var sketch = newSketch(context, id + "F16", { "sketchPlane" : qUnion([Q0])});
            skLineSegment(sketch, "E79.0", {"start": v(-70, 90) * mm, "end": v(70, 90) * mm});
            skArc(sketch, "E79.1", {"start": v(-70, 90) * mm, "mid": v(-77.07, 87.07) * mm, "end": v(-80, 80) * mm});
            skLineSegment(sketch, "E79.2", {"start": v(-80, -80) * mm, "end": v(-80, 80) * mm});
            skArc(sketch, "E79.3", {"start": v(-80, -80) * mm, "mid": v(-77.07, -87.07) * mm, "end": v(-70, -90) * mm});
            skLineSegment(sketch, "E79.4", {"start": v(-70, -90) * mm, "end": v(70, -90) * mm});
            skArc(sketch, "E79.5", {"start": v(70, -90) * mm, "mid": v(77.07, -87.07) * mm, "end": v(80, -80) * mm});
            skLineSegment(sketch, "E79.6", {"start": v(80, -80) * mm, "end": v(80, 80) * mm});
            skArc(sketch, "E79.7", {"start": v(80, 80) * mm, "mid": v(77.07, 87.07) * mm, "end": v(70, 90) * mm});
            skArc(sketch, "E79.8", {"start": v(56.15, 48.18) * mm, "mid": v(0, 67.5) * mm, "end": v(-56.15, 48.18) * mm});
            skArc(sketch, "E79.9", {"start": v(-56.15, 48.18) * mm, "mid": v(-58.99, 44.68) * mm, "end": v(-60, 40.3) * mm});
            skLineSegment(sketch, "E79.10", {"start": v(-60, 40.3) * mm, "end": v(-60, -40.3) * mm});
            skArc(sketch, "E79.11", {"start": v(-60, -40.3) * mm, "mid": v(-58.99, -44.68) * mm, "end": v(-56.15, -48.18) * mm});
            skArc(sketch, "E79.12", {"start": v(-56.15, -48.18) * mm, "mid": v(0, -67.5) * mm, "end": v(56.15, -48.18) * mm});
            skArc(sketch, "E79.13", {"start": v(56.15, -48.18) * mm, "mid": v(58.99, -44.68) * mm, "end": v(60, -40.3) * mm});
            skLineSegment(sketch, "E79.14", {"start": v(60, 40.3) * mm, "end": v(60, -40.3) * mm});
            skArc(sketch, "E79.15", {"start": v(60, 40.3) * mm, "mid": v(58.99, 44.68) * mm, "end": v(56.15, 48.18) * mm});
            skLineSegment(sketch, "E80", {"start": v(0, 90) * mm, "end": v(0, 120) * mm, "construction": true});
            skLineSegment(sketch, "E81", {"start": v(-33, 90) * mm, "end": v(-15, 108) * mm});
            skLineSegment(sketch, "E82", {"start": v(-15, 108) * mm, "end": v(-15, 120) * mm});
            skLineSegment(sketch, "E83", {"start": v(15, 108) * mm, "end": v(15, 120) * mm});
            skCircle(sketch, "E84", {"center": v(0, 120) * mm, "radius": 6 * mm});
            skArc(sketch, "E85", {"start": v(15, 120) * mm, "mid": v(0, 135) * mm, "end": v(-15, 120) * mm});
            skLineSegment(sketch, "E86", {"start": v(15, 108) * mm, "end": v(33, 90) * mm});
            skLineSegment(sketch, "E87", {"start": v(-80, 0) * mm, "end": v(80, 0) * mm, "construction": true});
            skLineSegment(sketch, "E88.MirrorCS", {"start": v(15, -108) * mm, "end": v(33, -90) * mm});
            skLineSegment(sketch, "E89.MirrorCS", {"start": v(15, -108) * mm, "end": v(15, -120) * mm});
            skArc(sketch, "E90.MirrorCS", {"start": v(15, -120) * mm, "mid": v(0, -135) * mm, "end": v(-15, -120) * mm});
            skLineSegment(sketch, "E91.MirrorCS", {"start": v(-15, -108) * mm, "end": v(-15, -120) * mm});
            skLineSegment(sketch, "E92.MirrorCS", {"start": v(-33, -90) * mm, "end": v(-15, -108) * mm});
            skLineSegment(sketch, "E93.MirrorCS", {"start": v(0, -90) * mm, "end": v(0, -120) * mm, "construction": true});
            skCircle(sketch, "E94.MirrorC", {"center": v(0, -120) * mm, "radius": 6 * mm});
            skSolve(sketch);
        }
        {
            var Q0;
            Q0 = qSketchRegion(id + "F16", true);
            var Q1;
            Q1=makeQuery(id+"F2.opExtrude","CAP_FACE",FACE,{"disambiguationData":[OSD([sQuery(id+"F0.wireOp",EDGE,"E12"),sQuery(id+"F0.wireOp",EDGE,"E13"),sQuery(id+"F0.wireOp",EDGE,"E14"),sQuery(id+"F0.wireOp",EDGE,"E15"),sQuery(id+"F0.wireOp",EDGE,"E17.filletArc"),sQuery(id+"F0.wireOp",EDGE,"E18.filletArc"),sQuery(id+"F0.wireOp",EDGE,"E19.filletArc"),sQuery(id+"F0.wireOp",EDGE,"E20.filletArc"),sQuery(id+"F0.wireOp",EDGE,"E25.0"),sQuery(id+"F0.wireOp",EDGE,"E25.1"),sQuery(id+"F0.wireOp",EDGE,"E25.2"),sQuery(id+"F0.wireOp",EDGE,"E25.3"),sQuery(id+"F0.wireOp",EDGE,"E25.4"),sQuery(id+"F0.wireOp",EDGE,"E25.5"),sQuery(id+"F0.wireOp",EDGE,"E25.6"),sQuery(id+"F0.wireOp",EDGE,"E25.7")])],"isStart":false});
            extrude(context, id + "F17", {"entities" : qUnion([Q0]), "endBound" : BoundingType.UP_TO_SURFACE, "endBoundEntityFace" : qUnion([Q1]), "depth" : 25 * mm});
        }
    });
